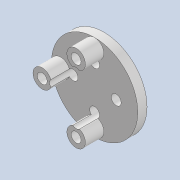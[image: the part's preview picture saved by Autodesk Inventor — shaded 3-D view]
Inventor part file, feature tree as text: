
AUTODESK INVENTOR PART (.ipt)
format: ipt  version: 2020 (Build 240168000, 168)  size: 240,640 bytes
history: native  units: mm
features: reference x6, other x4, extrude x3, sketch x3, plane x1, fillet x1, projected_geometry x1
ambient origin geometry x8: Origin, YZ Plane, XZ Plane, XY Plane, X Axis, Y Axis, Z Axis, Center Point
bodies: Solid1 (feature_tree)
feature tree (19):
  extrude  "Extrusion1"  Depth=3.0mm TaperAngle=0.0deg
  sketch  "Sketch2"  dims[d3=6.0mm d4=6.0mm]
  plane  "Work Plane1"
  extrude  "Extrusion2"  Depth=6.0mm
  extrude  "Extrusion3"  Depth=2.0mm TaperAngle=0.0deg
  fillet  "Fillet1"  Radius=4.0mm
  sketch  "Sketch1"  dims[d0=28.0mm d1=3.0mm d2=0.0mm]
  reference  "Reference1"
  reference  "Reference2"
  reference  "Reference3"
  reference  "Reference4"
  reference  "Reference5"
  reference  "Reference6"
  projected_geometry  "Projected Loop1"
  sketch  "Sketch3"  dims[d5=6.0mm d6=3.0mm d7=0.0mm d8=4.0mm d9=3.0mm d10=0.0mm d11=2.0mm]
  parser-record x1  (decoder bookkeeping rows leaked as tree rows — omitted from the tree; the rows remain in map.json)
  other  "driver_unit_1.iam"
  other  "driver_wheel_1:1"
  other  "tendon_wh_3:1"
note: 1 file-system path scrubbed to <path> (originals preserved in map.json)
